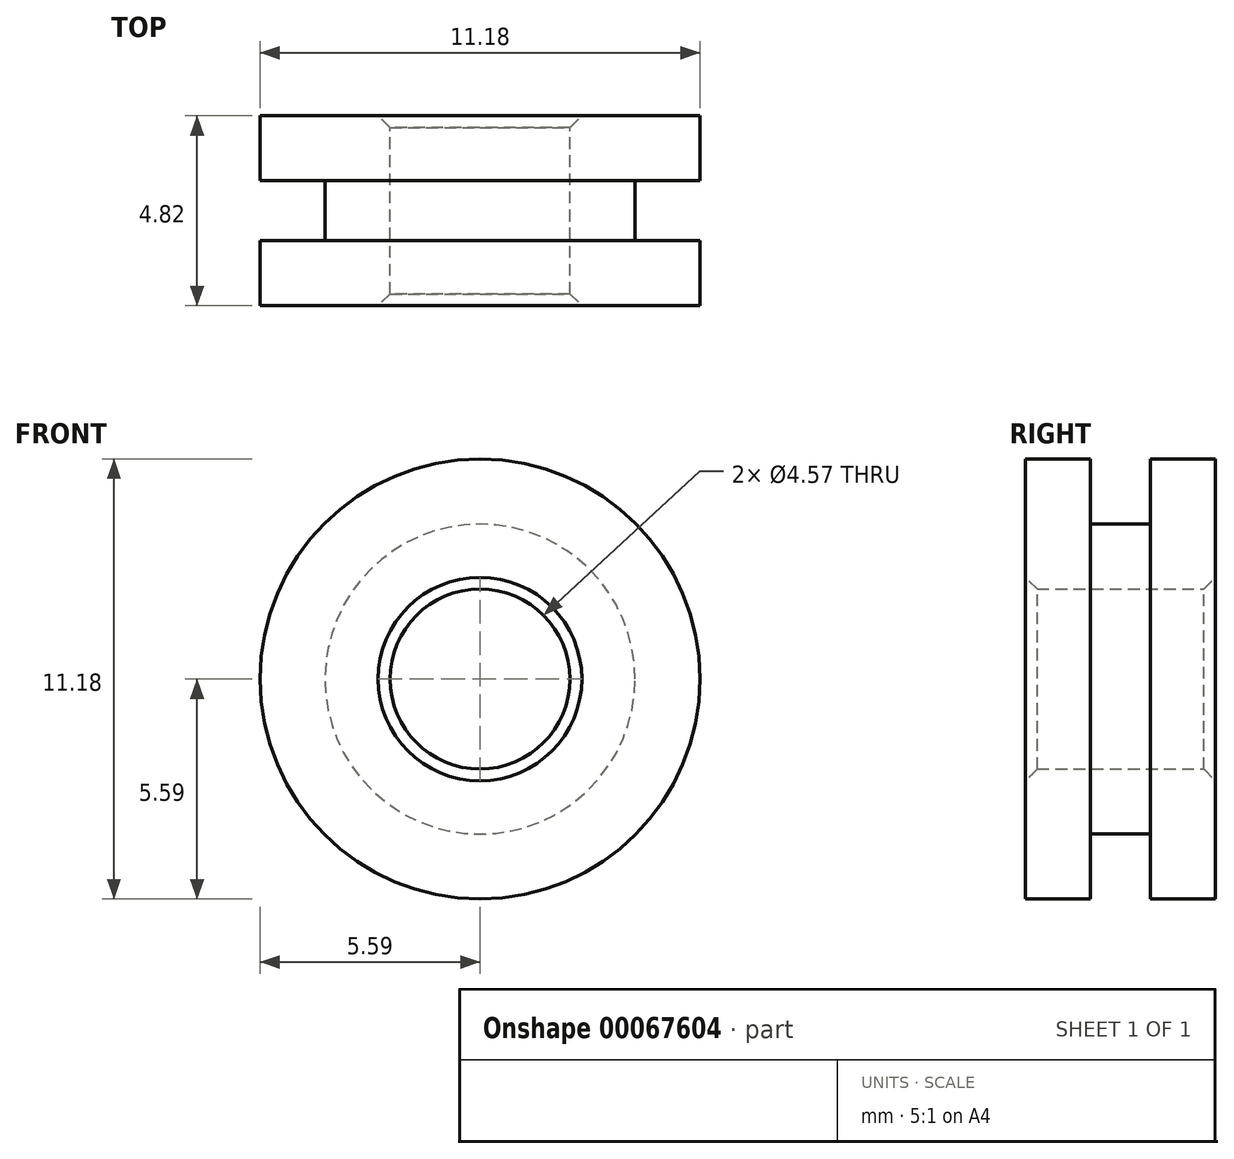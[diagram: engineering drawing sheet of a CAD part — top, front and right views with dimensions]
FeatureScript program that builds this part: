
annotation { "Feature Type Name" : "Feature", "Feature Type Description" : "" }
export const myFeature = defineFeature(function(context is Context, id is Id, definition is map)
    precondition{}
    {
        {
            var Q0;
            Q0=qCreatedBy(makeId("Front.planeOp"),FACE);
            var sketch = newSketch(context, id + "F0", { "sketchPlane" : qUnion([Q0])});
            skCircle(sketch, "E0", {"center": v(0, 0) * mm, "radius": 5.59 * mm});
            skCircle(sketch, "E1", {"center": v(0, 0) * mm, "radius": 2.29 * mm});
            skCircle(sketch, "E2", {"center": v(0, 0) * mm, "radius": 3.94 * mm});
            skSolve(sketch);
        }
        {
            var Q0;
            Q0=makeQuery(id+"F0.imprint","IMPRINT",FACE,{"disambiguationData":[TD([[makeQuery(id+"F0.imprint","IMPRINT",EDGE,{"derivedFrom":sQuery(id+"F0.wireOp",EDGE,"E1")}),-1.0]])]});
            var Q1;
            Q1=makeQuery(id+"F0.imprint","IMPRINT",FACE,{"disambiguationData":[TD([[makeQuery(id+"F0.imprint","IMPRINT",EDGE,{"derivedFrom":sQuery(id+"F0.wireOp",EDGE,"E0")}),1.0]])]});
            extrude(context, id + "F1", {"entities" : qUnion([Q0, Q1]), "endBound" : BoundingType.SYMMETRIC, "depth" : 4.83 * mm});
        }
        {
            var Q0;
            Q0 = qSketchRegion(id + "F0", true);
            extrude(context, id + "F2", {"entities" : qUnion([Q0]), "operationType" : NewBodyOperationType.REMOVE, "endBound" : BoundingType.SYMMETRIC, "oppositeDirection" : true, "depth" : 1.52 * mm});
        }
        {
            var Q0;
            Q0=makeQuery(id+"F1.opExtrude","CAP_EDGE",EDGE,{"disambiguationData":[OSD([sQuery(id+"F0.wireOp",EDGE,"E1")])],"isStart":false});
            var Q1;
            Q1=makeQuery(id+"F1.opExtrude","CAP_EDGE",EDGE,{"disambiguationData":[OSD([sQuery(id+"F0.wireOp",EDGE,"E1")])],"isStart":true});
            chamfer(context, id + "F3", {"entities" : qUnion([Q0, Q1]), "width" : .3 * mm, "tangentPropagation" : true});
        }
    });
